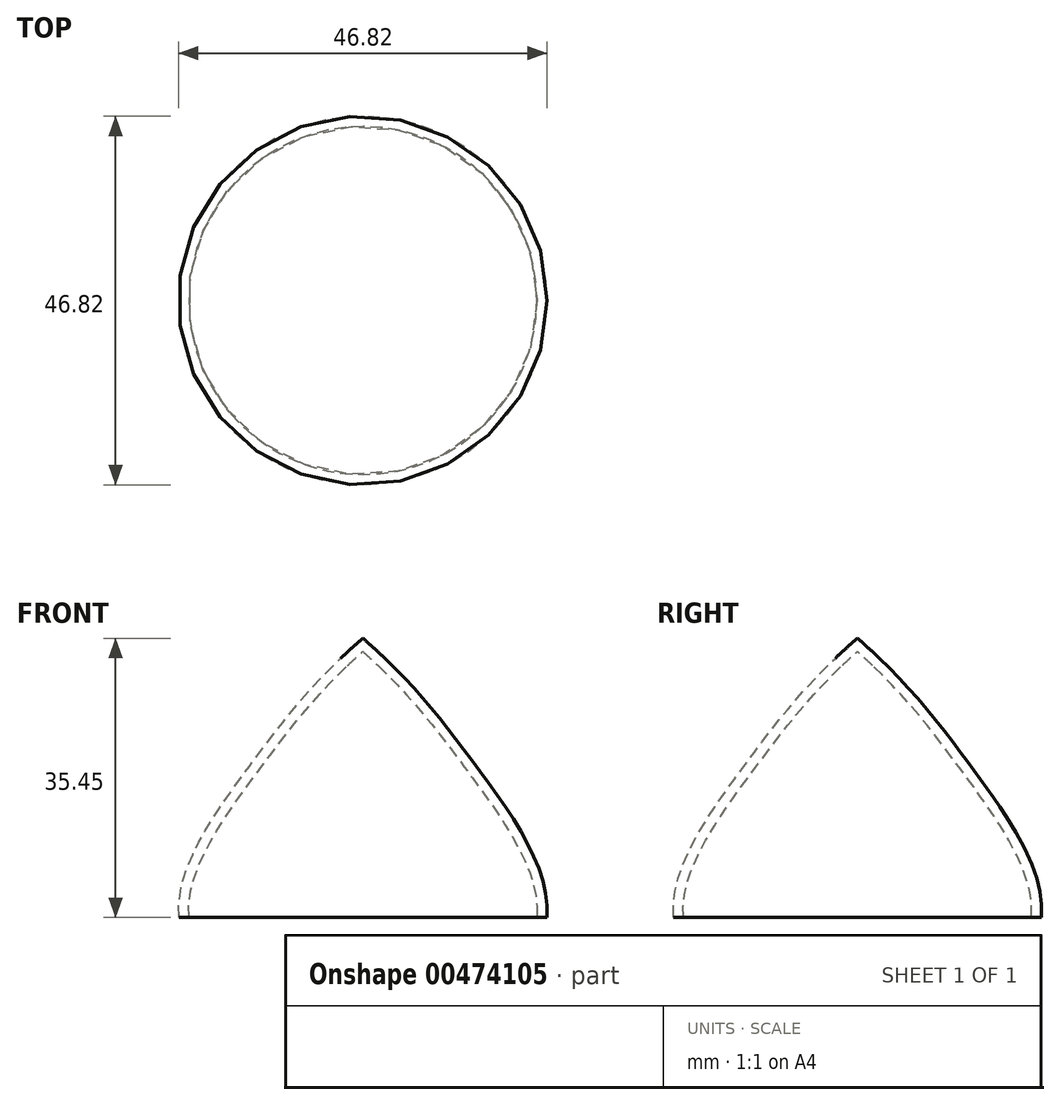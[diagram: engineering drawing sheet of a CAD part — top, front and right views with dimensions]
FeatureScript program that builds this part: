
annotation { "Feature Type Name" : "Feature", "Feature Type Description" : "" }
export const myFeature = defineFeature(function(context is Context, id is Id, definition is map)
    precondition{}
    {
        {
            var Q0;
            Q0=qCreatedBy(makeId("Front.planeOp"),FACE);
            var sketch = newSketch(context, id + "F0", { "sketchPlane" : qUnion([Q0])});
            skLineSegment(sketch, "E0", {"start": v(0, 35.45) * mm, "end": v(0, 0) * mm});
            skArc(sketch, "E1", {"start": v(3.4, 32) * mm, "mid": v(1.92, 33.94) * mm, "end": v(0, 35.45) * mm});
            skPoint(sketch, "E2.orphan", {"position": v(0, 35.45) * mm});
            skLineSegment(sketch, "E3", {"start": v(0, 0) * mm, "end": v(23.37, 0) * mm});
            skFitSpline(sketch, "E4", {"points": [v(0, 35.45) * mm, v(14.54, 19.01) * mm, v(23.37, 0) * mm], "startDerivative": vector(37.51, -32.34) * mm, "endDerivative": vector(-3.35, -37.63) * mm});
            skSolve(sketch);
        }
        {
            var Q0;
            {var subQ1=sQuery(id+"F0.wireOp",EDGE,"E0");Q0=makeQuery(id+"F0.imprint","IMPRINT",FACE,{"disambiguationData":[TD([[makeQuery(id+"F0.imprint","IMPRINT",EDGE,{"derivedFrom":subQ1}),1.0]])]});}
            var Q1;
            Q1=sQuery(id+"F0.wireOp",EDGE,"E0");
            revolve(context, id + "F1", {"entities" : qUnion([Q0]), "axis" : qUnion([Q1]), "revolveType" : RevolveType.FULL});
        }
        {
            var Q0;
            Q0=makeQuery(id+"F1.opRevolve","SWEPT_FACE",FACE,{"disambiguationData":[OSD([sQuery(id+"F0.wireOp",EDGE,"E3")])]});
            shell(context, id + "F2", {"entities" : qUnion([Q0]), "thickness" : 1.27 * mm});
        }
    });
